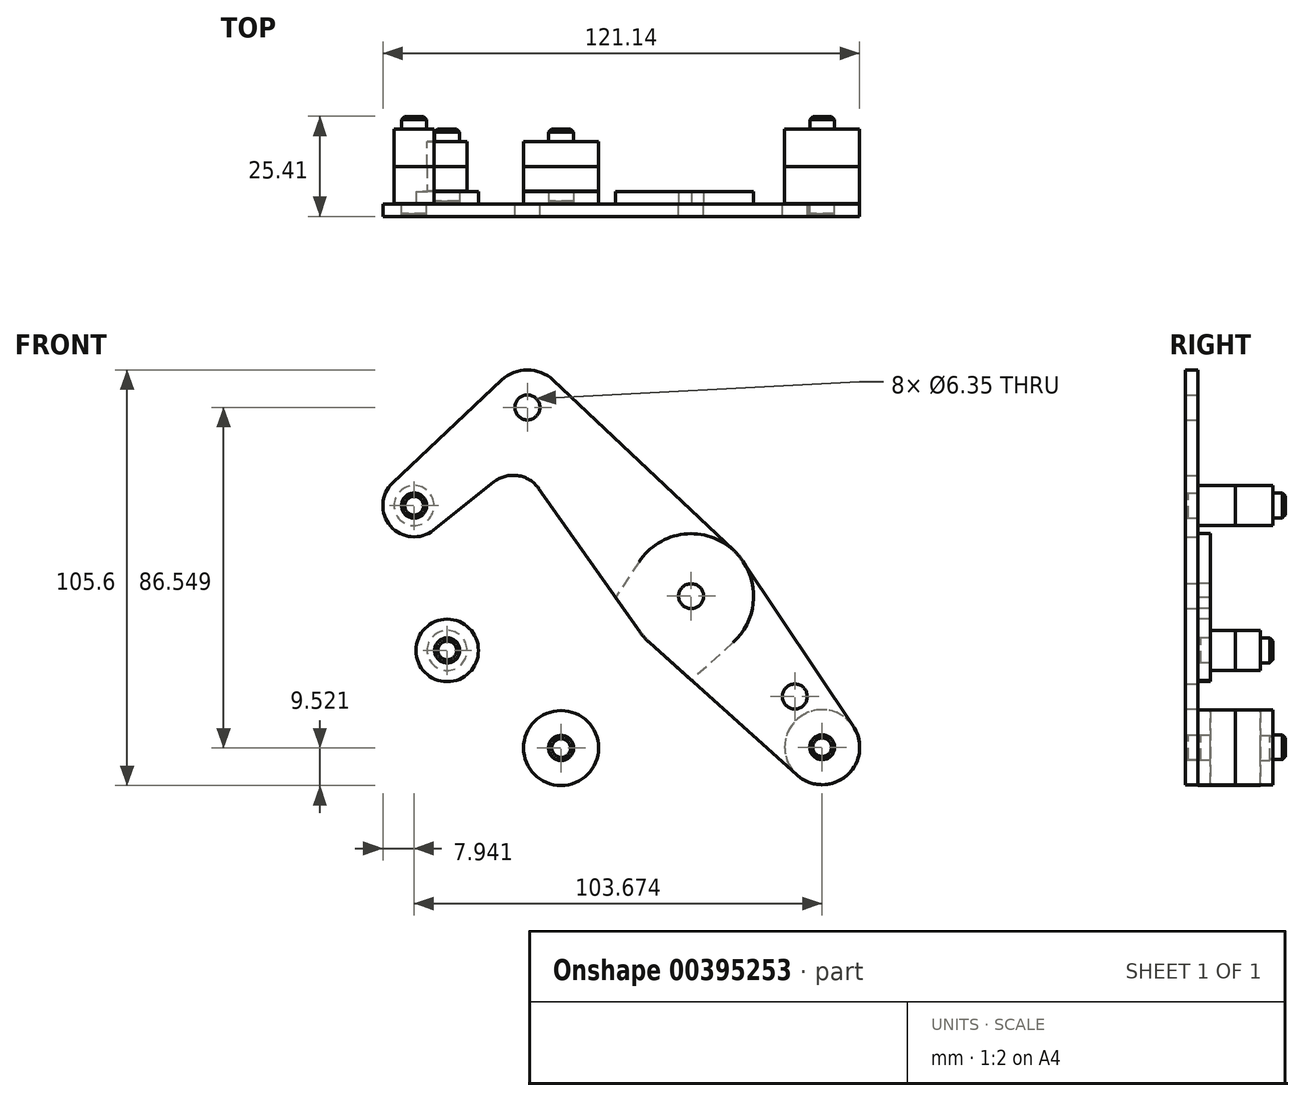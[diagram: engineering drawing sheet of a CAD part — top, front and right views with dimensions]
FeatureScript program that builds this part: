
annotation { "Feature Type Name" : "Feature", "Feature Type Description" : "" }
export const myFeature = defineFeature(function(context is Context, id is Id, definition is map)
    precondition{}
    {
        {
            var Q0;
            Q0=qCreatedBy(makeId("Front.planeOp"),FACE);
            var sketch = newSketch(context, id + "F0", { "sketchPlane" : qUnion([Q0])});
            skLineSegment(sketch, "E0", {"start": v(-41.6, 47.97) * mm, "end": v(41.6, -47.97) * mm, "construction": true});
            skCircle(sketch, "E1", {"center": v(0, 0) * mm, "radius": 3.18 * mm});
            skCircle(sketch, "E2", {"center": v(33.29, -38.38) * mm, "radius": 3.18 * mm});
            skCircle(sketch, "E3", {"center": v(-41.6, 47.97) * mm, "radius": 3.18 * mm});
            skCircle(sketch, "E4", {"center": v(-70.39, 23) * mm, "radius": 3.18 * mm});
            skLineSegment(sketch, "E5", {"start": v(-41.6, 47.97) * mm, "end": v(-70.39, 23) * mm, "construction": true});
            skCircle(sketch, "E6", {"center": v(33.29, -38.38) * mm, "radius": 9.53 * mm});
            skCircle(sketch, "E7", {"center": v(-70.39, 23) * mm, "radius": 7.94 * mm});
            skCircle(sketch, "E8", {"center": v(-41.6, 47.97) * mm, "radius": 9.53 * mm});
            skLineSegment(sketch, "E9", {"start": v(-75.83, 28.78) * mm, "end": v(-48.14, 54.9) * mm});
            skLineSegment(sketch, "E10", {"start": v(-65.44, 16.8) * mm, "end": v(-50.15, 28.98) * mm});
            skCircle(sketch, "E11", {"center": v(0, 0) * mm, "radius": 15.88 * mm});
            skLineSegment(sketch, "E12", {"start": v(-35.07, 54.9) * mm, "end": v(10.9, 11.55) * mm});
            skLineSegment(sketch, "E13", {"start": v(-38.72, 27.35) * mm, "end": v(-12.97, -9.15) * mm});
            skLineSegment(sketch, "E14", {"start": v(-10.6, -11.82) * mm, "end": v(26.93, -45.47) * mm});
            skLineSegment(sketch, "E15", {"start": v(13.2, 8.82) * mm, "end": v(41.2, -33.08) * mm});
            skArc(sketch, "E16.filletArc", {"start": v(-38.72, 27.35) * mm, "mid": v(-44.08, 30.63) * mm, "end": v(-50.15, 28.98) * mm});
            skLineSegment(sketch, "E17", {"start": v(0, 0) * mm, "end": v(-33.05, -38.58) * mm, "construction": true});
            skLineSegment(sketch, "E18", {"start": v(-33.05, -38.58) * mm, "end": v(-61.98, -13.8) * mm, "construction": true});
            skCircle(sketch, "E19", {"center": v(-61.98, -13.8) * mm, "radius": 3.18 * mm});
            skCircle(sketch, "E20", {"center": v(-33.05, -38.58) * mm, "radius": 3.18 * mm});
            skCircle(sketch, "E21", {"center": v(-61.98, -13.8) * mm, "radius": 7.94 * mm});
            skCircle(sketch, "E22", {"center": v(-33.05, -38.58) * mm, "radius": 9.53 * mm});
            skLineSegment(sketch, "E23", {"start": v(-57.08, -7.55) * mm, "end": v(-42.08, -19.35) * mm});
            skLineSegment(sketch, "E24", {"start": v(-67.4, -19.6) * mm, "end": v(-39.54, -45.55) * mm});
            skLineSegment(sketch, "E25", {"start": v(-13.25, 8.74) * mm, "end": v(-30.55, -17.48) * mm});
            skLineSegment(sketch, "E26", {"start": v(10.67, -11.75) * mm, "end": v(-26.65, -45.63) * mm});
            skArc(sketch, "E27.filletArc", {"start": v(-42.08, -19.35) * mm, "mid": v(-35.9, -20.95) * mm, "end": v(-30.55, -17.48) * mm});
            skCircle(sketch, "E28", {"center": v(-19.62, -22.9) * mm, "radius": 3.18 * mm});
            skCircle(sketch, "E29", {"center": v(26.32, -25.5) * mm, "radius": 3.18 * mm});
            skLineSegment(sketch, "E30", {"start": v(26.32, -25.5) * mm, "end": v(23.92, -27.58) * mm, "construction": true});
            skCircle(sketch, "E31", {"center": v(0, 0) * mm, "radius": 3.97 * mm});
            skSolve(sketch);
        }
        {
            var Q0;
            Q0=qCreatedBy(makeId("Front.planeOp"),FACE);
            cPlane(context, id + "F1", {"entities" : qUnion([Q0]), "cplaneType" : CPlaneType.OFFSET, "offset" : 9.52 * mm, "oppositeDirection" : true, "width" : 254 * mm, "height" : 254 * mm});
        }
        {
            var Q0;
            Q0=makeQuery(id+"F0.imprint","IMPRINT",FACE,{"disambiguationData":[TD([[makeQuery(id+"F0.imprint","IMPRINT",EDGE,{"derivedFrom":sQuery(id+"F0.wireOp",EDGE,"E2")}),-1.0]])]});
            var Q1;
            Q1=makeQuery(id+"F0.imprint","IMPRINT",FACE,{"disambiguationData":[TD([[makeQuery(id+"F0.imprint","IMPRINT",EDGE,{"derivedFrom":sQuery(id+"F0.wireOp",EDGE,"E3")}),-1.0]])]});
            var Q2;
            Q2=makeQuery(id+"F0.imprint","IMPRINT",FACE,{"disambiguationData":[TD([[makeQuery(id+"F0.imprint","IMPRINT",EDGE,{"derivedFrom":sQuery(id+"F0.wireOp",EDGE,"E4")}),-1.0]])]});
            var Q3;
            {var subQ0=sQuery(id+"F0.wireOp",EDGE,"E13");var subQ1=sQuery(id+"F0.wireOp",EDGE,"E11");var subQ2=makeQuery(id+"F0.imprint","INTERSECT",VERTEX,{"derivedFrom":[subQ1,subQ0]});Q3=makeQuery(id+"F0.imprint","IMPRINT",FACE,{"disambiguationData":[TD([[makeQuery(id+"F0.imprint","IMPRINT",EDGE,{"disambiguationData":[TD([[subQ2,1.0]])],"derivedFrom":subQ1}),-1.0]])]});}
            var Q4;
            {var subQ0=sQuery(id+"F0.wireOp",EDGE,"E14");var subQ1=sQuery(id+"F0.wireOp",EDGE,"E11");var subQ2=makeQuery(id+"F0.imprint","INTERSECT",VERTEX,{"derivedFrom":[subQ1,subQ0]});Q4=makeQuery(id+"F0.imprint","IMPRINT",FACE,{"disambiguationData":[TD([[makeQuery(id+"F0.imprint","IMPRINT",EDGE,{"disambiguationData":[TD([[subQ2,-1.0]])],"derivedFrom":subQ1}),-1.0]])]});}
            var Q5;
            {var subQ0=sQuery(id+"F0.wireOp",EDGE,"E15");Q5=makeQuery(id+"F0.imprint","IMPRINT",FACE,{"disambiguationData":[TD([[makeQuery(id+"F0.imprint","IMPRINT",EDGE,{"derivedFrom":subQ0}),-1.0]])]});}
            var Q6;
            {var subQ0=sQuery(id+"F0.wireOp",EDGE,"E9");Q6=makeQuery(id+"F0.imprint","IMPRINT",FACE,{"disambiguationData":[TD([[makeQuery(id+"F0.imprint","IMPRINT",EDGE,{"derivedFrom":subQ0}),-1.0]])]});}
            var Q7;
            Q7=makeQuery(id+"F0.imprint","IMPRINT",FACE,{"disambiguationData":[TD([[makeQuery(id+"F0.imprint","IMPRINT",EDGE,{"derivedFrom":sQuery(id+"F0.wireOp",EDGE,"E31")}),-1.0]])]});
            var Q8;
            Q8=makeQuery(id+"F0.imprint","IMPRINT",FACE,{"disambiguationData":[TD([[makeQuery(id+"F0.imprint","IMPRINT",EDGE,{"derivedFrom":sQuery(id+"F0.wireOp",EDGE,"E1")}),-1.0]])]});
            extrude(context, id + "F2", {"entities" : qUnion([Q0, Q1, Q2, Q3, Q4, Q5, Q6, Q7, Q8]), "depth" : 3.17 * mm});
        }
        {
            var Q0;
            Q0=makeQuery(id+"F0.imprint","IMPRINT",FACE,{"disambiguationData":[TD([[makeQuery(id+"F0.imprint","IMPRINT",EDGE,{"derivedFrom":sQuery(id+"F0.wireOp",EDGE,"E31")}),-1.0]])]});
            var Q1;
            {var subQ0=sQuery(id+"F0.wireOp",EDGE,"E13");var subQ1=sQuery(id+"F0.wireOp",EDGE,"E11");var subQ2=makeQuery(id+"F0.imprint","INTERSECT",VERTEX,{"derivedFrom":[subQ1,subQ0]});Q1=makeQuery(id+"F0.imprint","IMPRINT",FACE,{"disambiguationData":[TD([[makeQuery(id+"F0.imprint","IMPRINT",EDGE,{"disambiguationData":[TD([[subQ2,1.0]])],"derivedFrom":subQ1}),-1.0]])]});}
            var Q2;
            {var subQ0=sQuery(id+"F0.wireOp",EDGE,"E14");var subQ1=sQuery(id+"F0.wireOp",EDGE,"E11");var subQ2=makeQuery(id+"F0.imprint","INTERSECT",VERTEX,{"derivedFrom":[subQ1,subQ0]});Q2=makeQuery(id+"F0.imprint","IMPRINT",FACE,{"disambiguationData":[TD([[makeQuery(id+"F0.imprint","IMPRINT",EDGE,{"disambiguationData":[TD([[subQ2,-1.0]])],"derivedFrom":subQ1}),-1.0]])]});}
            var Q3;
            Q3=makeQuery(id+"F0.imprint","IMPRINT",FACE,{"disambiguationData":[TD([[makeQuery(id+"F0.imprint","IMPRINT",EDGE,{"derivedFrom":sQuery(id+"F0.wireOp",EDGE,"E20")}),-1.0]])]});
            var Q4;
            Q4=makeQuery(id+"F0.imprint","IMPRINT",FACE,{"disambiguationData":[TD([[makeQuery(id+"F0.imprint","IMPRINT",EDGE,{"derivedFrom":sQuery(id+"F0.wireOp",EDGE,"E19")}),-1.0]])]});
            var Q5;
            {var subQ13=sQuery(id+"F0.wireOp",EDGE,"E23");Q5=makeQuery(id+"F0.imprint","IMPRINT",FACE,{"disambiguationData":[TD([[makeQuery(id+"F0.imprint","IMPRINT",EDGE,{"derivedFrom":subQ13}),-1.0]])]});}
            var Q6;
            Q6=makeQuery(id+"F0.imprint","IMPRINT",FACE,{"disambiguationData":[TD([[makeQuery(id+"F0.imprint","IMPRINT",EDGE,{"derivedFrom":sQuery(id+"F0.wireOp",EDGE,"E1")}),-1.0]])]});
            extrude(context, id + "F3", {"entities" : qUnion([Q0, Q1, Q2, Q3, Q4, Q5, Q6]), "oppositeDirection" : true, "depth" : 3.17 * mm});
        }
        {
            var Q0;
            Q0=makeQuery(id+"F2.opExtrude","CAP_FACE",FACE,{"disambiguationData":[OSD([sQuery(id+"F0.wireOp",EDGE,"E1"),sQuery(id+"F0.wireOp",EDGE,"E2"),sQuery(id+"F0.wireOp",EDGE,"E3"),sQuery(id+"F0.wireOp",EDGE,"E4"),sQuery(id+"F0.wireOp",EDGE,"E6"),sQuery(id+"F0.wireOp",EDGE,"E7"),sQuery(id+"F0.wireOp",EDGE,"E8"),sQuery(id+"F0.wireOp",EDGE,"E9"),sQuery(id+"F0.wireOp",EDGE,"E10"),sQuery(id+"F0.wireOp",EDGE,"E11"),sQuery(id+"F0.wireOp",EDGE,"E12"),sQuery(id+"F0.wireOp",EDGE,"E13"),sQuery(id+"F0.wireOp",EDGE,"E14"),sQuery(id+"F0.wireOp",EDGE,"E15"),sQuery(id+"F0.wireOp",EDGE,"E16.filletArc"),sQuery(id+"F0.wireOp",EDGE,"E29")])],"isStart":false});
            var sketch = newSketch(context, id + "F4", { "sketchPlane" : qUnion([Q0])});
            skCircle(sketch, "E32", {"center": v(33.29, -38.38) * mm, "radius": 9.53 * mm});
            skCircle(sketch, "E33", {"center": v(-70.39, 23) * mm, "radius": 5.08 * mm});
            skSolve(sketch);
        }
        {
            var Q0;
            Q0=makeQuery(id+"F3.opExtrude","CAP_FACE",FACE,{"disambiguationData":[OSD([sQuery(id+"F0.wireOp",EDGE,"E1"),sQuery(id+"F0.wireOp",EDGE,"E11"),sQuery(id+"F0.wireOp",EDGE,"E19"),sQuery(id+"F0.wireOp",EDGE,"E20"),sQuery(id+"F0.wireOp",EDGE,"E21"),sQuery(id+"F0.wireOp",EDGE,"E22"),sQuery(id+"F0.wireOp",EDGE,"E23"),sQuery(id+"F0.wireOp",EDGE,"E24"),sQuery(id+"F0.wireOp",EDGE,"E25"),sQuery(id+"F0.wireOp",EDGE,"E26"),sQuery(id+"F0.wireOp",EDGE,"E27.filletArc"),sQuery(id+"F0.wireOp",EDGE,"E28")])],"isStart":true});
            var sketch = newSketch(context, id + "F5", { "sketchPlane" : qUnion([Q0])});
            skCircle(sketch, "E34", {"center": v(-33.05, -38.58) * mm, "radius": 9.53 * mm});
            skCircle(sketch, "E35", {"center": v(-61.98, -13.8) * mm, "radius": 5.08 * mm});
            skSolve(sketch);
        }
        {
            var Q0;
            Q0 = qSketchRegion(id + "F4", true);
            var Q1;
            Q1 = qSketchRegion(id + "F5", true);
            var Q2;
            Q2=qCreatedBy(id+"F1.planeOp",FACE);
            extrude(context, id + "F6", {"entities" : qUnion([Q0, Q1]), "endBound" : BoundingType.UP_TO_SURFACE, "oppositeDirection" : true, "endBoundEntityFace" : qUnion([Q2]), "depth" : 25.4 * mm});
        }
        {
            var Q0;
            Q0=makeQuery(id+"F2.opExtrude","SWEPT_BODY",BODY,{"disambiguationData":[OSD([sQuery(id+"F0.wireOp",EDGE,"E1"),sQuery(id+"F0.wireOp",EDGE,"E2"),sQuery(id+"F0.wireOp",EDGE,"E3"),sQuery(id+"F0.wireOp",EDGE,"E4"),sQuery(id+"F0.wireOp",EDGE,"E6"),sQuery(id+"F0.wireOp",EDGE,"E7"),sQuery(id+"F0.wireOp",EDGE,"E8"),sQuery(id+"F0.wireOp",EDGE,"E9"),sQuery(id+"F0.wireOp",EDGE,"E10"),sQuery(id+"F0.wireOp",EDGE,"E11"),sQuery(id+"F0.wireOp",EDGE,"E12"),sQuery(id+"F0.wireOp",EDGE,"E13"),sQuery(id+"F0.wireOp",EDGE,"E14"),sQuery(id+"F0.wireOp",EDGE,"E15"),sQuery(id+"F0.wireOp",EDGE,"E16.filletArc"),sQuery(id+"F0.wireOp",EDGE,"E29")])]});
            var Q1;
            Q1=makeQuery(id+"F3.opExtrude","SWEPT_BODY",BODY,{"disambiguationData":[OSD([sQuery(id+"F0.wireOp",EDGE,"E1"),sQuery(id+"F0.wireOp",EDGE,"E11"),sQuery(id+"F0.wireOp",EDGE,"E19"),sQuery(id+"F0.wireOp",EDGE,"E20"),sQuery(id+"F0.wireOp",EDGE,"E21"),sQuery(id+"F0.wireOp",EDGE,"E22"),sQuery(id+"F0.wireOp",EDGE,"E23"),sQuery(id+"F0.wireOp",EDGE,"E24"),sQuery(id+"F0.wireOp",EDGE,"E25"),sQuery(id+"F0.wireOp",EDGE,"E26"),sQuery(id+"F0.wireOp",EDGE,"E27.filletArc"),sQuery(id+"F0.wireOp",EDGE,"E28")])]});
            var Q2;
            Q2=makeQuery(id+"F6.opExtrude","SWEPT_BODY",BODY,{"disambiguationData":[OSD([sQuery(id+"F4.wireOp",EDGE,"E32")])]});
            var Q3;
            Q3=makeQuery(id+"F6.opExtrude","SWEPT_BODY",BODY,{"disambiguationData":[OSD([sQuery(id+"F5.wireOp",EDGE,"E34")])]});
            var Q4;
            Q4=makeQuery(id+"F6.opExtrude","SWEPT_BODY",BODY,{"disambiguationData":[OSD([sQuery(id+"F5.wireOp",EDGE,"E35")])]});
            var Q5;
            Q5=makeQuery(id+"F6.opExtrude","SWEPT_BODY",BODY,{"disambiguationData":[OSD([sQuery(id+"F4.wireOp",EDGE,"E33")])]});
            booleanBodies(context, id + "F7", {"operationType" : BooleanOperationType.SUBTRACTION, "tools" : qUnion([Q0, Q1]), "targets" : qUnion([Q2, Q3, Q4, Q5]), "offset" : true, "offsetAll" : true, "offsetDistance" : 0.03 * mm, "keepTools" : true});
        }
        {
            var Q0;
            Q0=makeQuery(id+"F7.tempBoolean.opBoolean","INTERSECT",EDGE,{"derivedFrom":[makeQuery(id+"F6.opExtrude","CAP_FACE",FACE,{"disambiguationData":[OSD([sQuery(id+"F4.wireOp",EDGE,"E32")])],"isStart":true}),makeQuery(id+"F7.offsetTempBody.opPattern","COPY",FACE,{"derivedFrom":makeQuery(id+"F2.opExtrude","SWEPT_FACE",FACE,{"disambiguationData":[OSD([sQuery(id+"F0.wireOp",EDGE,"E2")])]}),"instanceName":"1"})]});
            var Q1;
            Q1=makeQuery(id+"F6.opExtrude","CAP_FACE",FACE,{"disambiguationData":[OSD([sQuery(id+"F5.wireOp",EDGE,"E34")])],"isStart":true});
            var Q2;
            Q2=makeQuery(id+"F6.opExtrude","CAP_FACE",FACE,{"disambiguationData":[OSD([sQuery(id+"F5.wireOp",EDGE,"E35")])],"isStart":true});
            var Q3;
            Q3=makeQuery(id+"F6.opExtrude","CAP_FACE",FACE,{"disambiguationData":[OSD([sQuery(id+"F4.wireOp",EDGE,"E33")])],"isStart":true});
            chamfer(context, id + "F8", {"entities" : qUnion([Q0, Q1, Q2, Q3]), "width" : 0.76 * mm, "tangentPropagation" : true});
        }
        {
            var Q0;
            Q0=makeQuery(id+"F6.opExtrude","SWEPT_BODY",BODY,{"disambiguationData":[OSD([sQuery(id+"F5.wireOp",EDGE,"E35")])]});
            var Q1;
            Q1=makeQuery(id+"F6.opExtrude","SWEPT_BODY",BODY,{"disambiguationData":[OSD([sQuery(id+"F5.wireOp",EDGE,"E34")])]});
            var Q2;
            Q2=makeQuery(id+"F6.opExtrude","SWEPT_BODY",BODY,{"disambiguationData":[OSD([sQuery(id+"F4.wireOp",EDGE,"E33")])]});
            var Q3;
            Q3=makeQuery(id+"F6.opExtrude","SWEPT_BODY",BODY,{"disambiguationData":[OSD([sQuery(id+"F4.wireOp",EDGE,"E32")])]});
            var Q4;
            Q4=qCreatedBy(id+"F1.planeOp",FACE);
            mirror(context, id + "F9", {"operationType" : NewBodyOperationType.ADD, "entities" : qUnion([Q0, Q1, Q2, Q3]), "mirrorPlane" : qUnion([Q4])});
        }
    });
